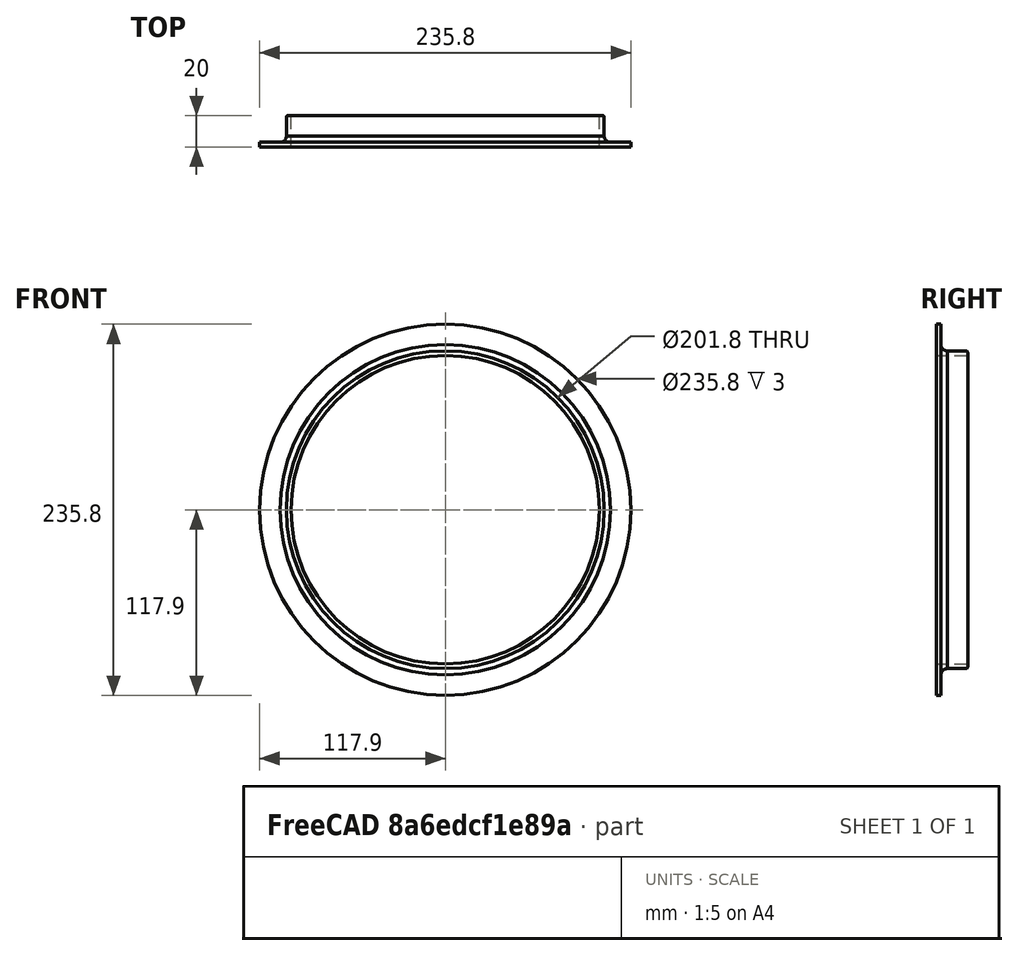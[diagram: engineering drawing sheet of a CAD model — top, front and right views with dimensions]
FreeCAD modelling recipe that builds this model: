
FCSTD DOCUMENT  (FreeCAD 0.18R16110 (Git))
Label: 8inducking
License: All rights reserved
LicenseURL: http://en.wikipedia.org/wiki/All_rights_reserved
objects: Sketcher::SketchObject×1, Part::Revolution×1, Part::Fillet×1
note: 3 computed .brp shape members not serialized (recipe doc carries the construction recipe); baked Part::Feature solids carry a one-line shape summary decoded from their .brp

FEATURE [Sketcher::SketchObject] Sketch
  sketch-geometry (7):
    g0: LineSegment StartX=97.9 StartY=0 StartZ=0 EndX=97.9 EndY=20 EndZ=0
    g1: LineSegment StartX=97.9 StartY=20 StartZ=0 EndX=100.9 EndY=20 EndZ=0
    g2: LineSegment StartX=97.9 StartY=0 StartZ=0 EndX=117.9 EndY=0 EndZ=0
    g3: LineSegment StartX=117.9 StartY=0 StartZ=0 EndX=117.9 EndY=3 EndZ=0
    g4: LineSegment StartX=117.9 StartY=3 StartZ=0 EndX=104.9 EndY=3 EndZ=0
    g5: LineSegment StartX=100.9 StartY=20 StartZ=0 EndX=100.9 EndY=7 EndZ=0
    g6: ArcOfCircle CenterX=104.989 CenterY=7.08903 CenterZ=0 NormalX=0 NormalY=0 NormalZ=1 AngleXU=0 Radius=4.09 StartAngle=3.16336 EndAngle=4.69062
  constraints (22):
    c: PointOnObject(g0,g-1)
    c: Vertical(g0)
    c: DistanceX(g0) = 97.9
    c: DistanceY(g0) = 20
    c: Coincident(g1,g0)
    c: Horizontal(g1)
    c: DistanceX(g1,g1) = 3
    c: Coincident(g0,g2)
    c: PointOnObject(g2,g-1)
    c: Coincident(g2,g3)
    c: Vertical(g3)
    c: Coincident(g3,g4)
    c: Coincident(g5,g1)
    c: Vertical(g5)
    c: Coincident(g6,g5)
    c: Coincident(g6,g4)
    c: Horizontal(g4)
    c: DistanceY(g3,g3) = 3
    c: DistanceX(g4,g4) = 13
    c: DistanceY(g5,g5) = 13
    c: Radius(g6) = 4.09
    c: DistanceX(g2,g2) = 20
FEATURE [Part::Revolution] Revolve
  Angle = 360
  Axis = (0,1,0)
  Base = (0,0,0)
  FaceMakerClass = Part::FaceMakerBullseye
  Solid = false
  Source = -> Sketch
  Symmetric = false
FEATURE [Part::Fillet] Fillet
  Base = -> Revolve
  Edges = 1 edges r=1: [Edge4]
